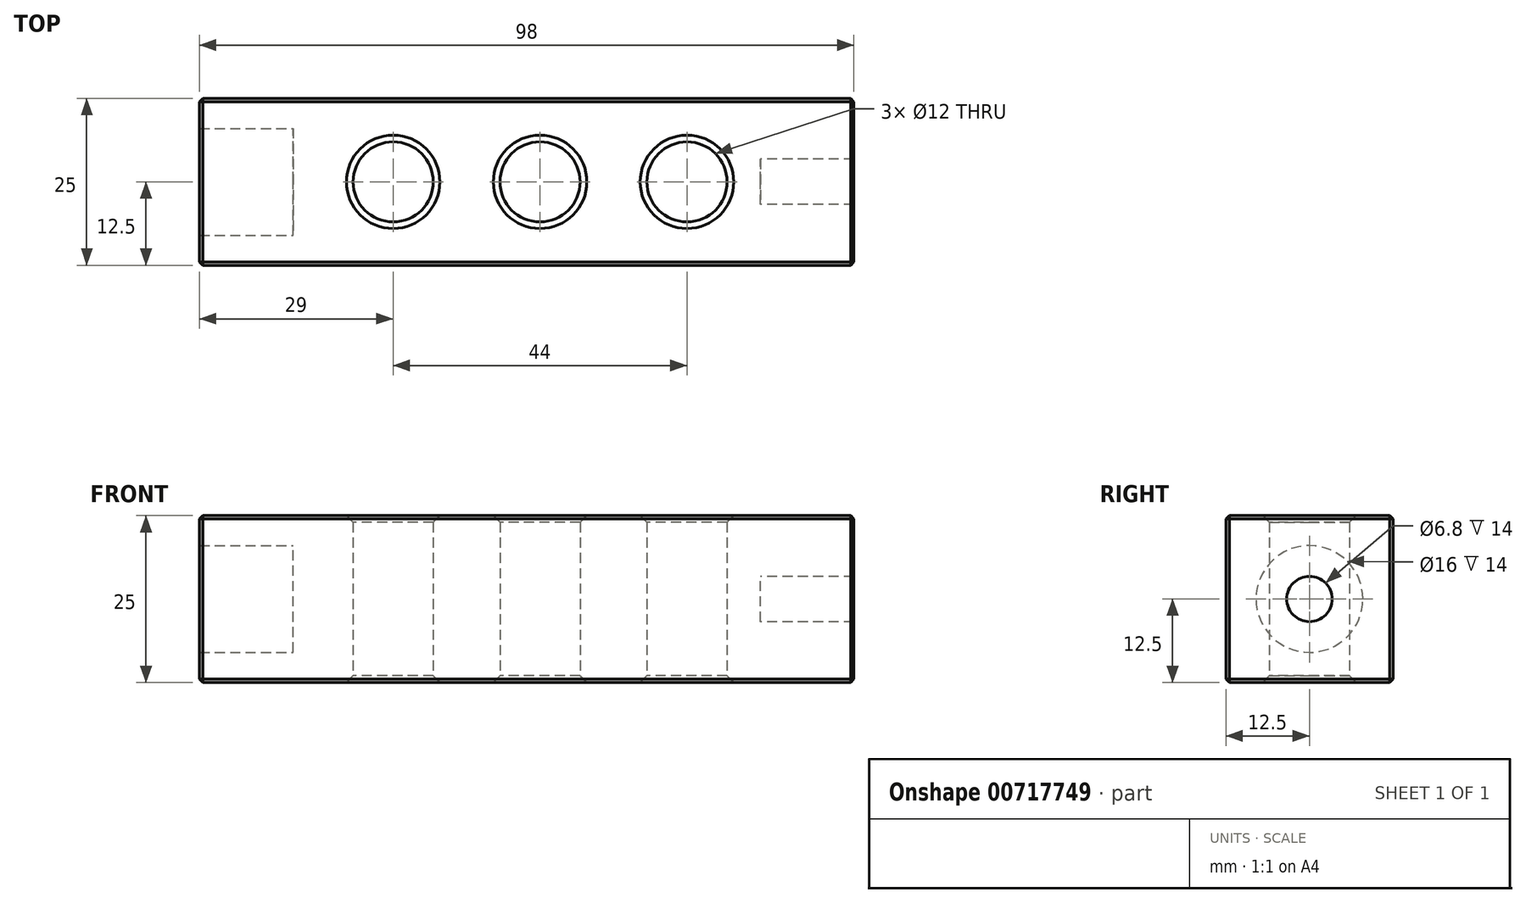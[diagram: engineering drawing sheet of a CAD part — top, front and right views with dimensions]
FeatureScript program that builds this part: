
annotation { "Feature Type Name" : "Feature", "Feature Type Description" : "" }
export const myFeature = defineFeature(function(context is Context, id is Id, definition is map)
    precondition{}
    {
        {
            var Q0;
            Q0=qCreatedBy(makeId("Top.planeOp"),FACE);
            var sketch = newSketch(context, id + "F0", { "sketchPlane" : qUnion([Q0])});
            skLineSegment(sketch, "E0.bottom", {"start": v(49, 12.5) * mm, "end": v(-49, 12.5) * mm});
            skLineSegment(sketch, "E0.top", {"start": v(49, -12.5) * mm, "end": v(-49, -12.5) * mm});
            skLineSegment(sketch, "E0.left", {"start": v(49, 12.5) * mm, "end": v(49, -12.5) * mm});
            skLineSegment(sketch, "E0.right", {"start": v(-49, 12.5) * mm, "end": v(-49, -12.5) * mm});
            skPoint(sketch, "E0.middle", {"position": v(0, 0) * mm});
            skLineSegment(sketch, "E1", {"start": v(49, 0) * mm, "end": v(-49, 0) * mm, "construction": true});
            skLineSegment(sketch, "E2", {"start": v(49, 12.5) * mm, "end": v(49, 22.83) * mm, "construction": true});
            skLineSegment(sketch, "E3", {"start": v(49, 22.83) * mm, "end": v(24, 22.83) * mm, "construction": true});
            skLineSegment(sketch, "E4", {"start": v(24, 22.83) * mm, "end": v(24, -3.88) * mm, "construction": true});
            skCircle(sketch, "E5", {"center": v(24, 0) * mm, "radius": 6 * mm});
            skCircle(sketch, "E6.1.0.0", {"center": v(2, 0) * mm, "radius": 6 * mm});
            skCircle(sketch, "E6.2.0.0", {"center": v(-20, 0) * mm, "radius": 6 * mm});
            skLineSegment(sketch, "E6.direction1", {"start": v(24, 0) * mm, "end": v(2, 0) * mm, "construction": true});
            skSolve(sketch);
        }
        {
            var Q0;
            Q0=makeQuery(id+"F0.imprint","IMPRINT",FACE,{"disambiguationData":[TD([[makeQuery(id+"F0.imprint","IMPRINT",EDGE,{"derivedFrom":sQuery(id+"F0.wireOp",EDGE,"E0.bottom")}),1.0]])]});
            extrude(context, id + "F1", {"entities" : qUnion([Q0]), "depth" : 25 * mm});
        }
        {
            var Q0;
            Q0=qCreatedBy(makeId("Right.planeOp"),FACE);
            var sketch = newSketch(context, id + "F2", { "sketchPlane" : qUnion([Q0])});
            skLineSegment(sketch, "E7", {"start": v(0, 0) * mm, "end": v(0, 12.5) * mm, "construction": true});
            skCircle(sketch, "E8", {"center": v(0, 12.5) * mm, "radius": 3.4 * mm});
            skSolve(sketch);
        }
        {
            var Q0;
            Q0=qSketchRegion(id+"F2",true);
            extrude(context, id + "F3", {"entities" : qUnion([Q0]), "operationType" : NewBodyOperationType.REMOVE, "depth" : 120 * mm, "hasSecondDirection" : true, "secondDirectionOppositeDirection" : true, "secondDirectionDepth" : -35 * mm, "offsetDistance" : 25 * mm});
        }
        {
            var Q0;
            Q0=qCreatedBy(makeId("Top.planeOp"),FACE);
            cPlane(context, id + "F4", {"entities" : qUnion([Q0]), "cplaneType" : CPlaneType.OFFSET, "offset" : 12.5 * mm, "width" : 150 * mm, "height" : 150 * mm});
        }
        {
            var Q0;
            Q0=qCreatedBy(id+"F4.planeOp",FACE);
            var sketch = newSketch(context, id + "F5", { "sketchPlane" : qUnion([Q0])});
            skLineSegment(sketch, "E9", {"start": v(0, 0) * mm, "end": v(100, 0) * mm, "construction": true});
            skArc(sketch, "E10", {"start": v(112.5, 0) * mm, "mid": v(100, 12.5) * mm, "end": v(87.5, 0) * mm});
            skLineSegment(sketch, "E11", {"start": v(100, 0) * mm, "end": v(112.5, 0) * mm});
            skLineSegment(sketch, "E12", {"start": v(100, 0) * mm, "end": v(87.5, 0) * mm});
            skSolve(sketch);
        }
        {
            var Q0;
            Q0=qCreatedBy(makeId("Right.planeOp"),FACE);
            var sketch = newSketch(context, id + "F6", { "sketchPlane" : qUnion([Q0])});
            skLineSegment(sketch, "E13", {"start": v(0, 0) * mm, "end": v(0, 12.5) * mm, "construction": true});
            skCircle(sketch, "E14", {"center": v(0, 12.5) * mm, "radius": 8 * mm});
            skSolve(sketch);
        }
        {
            var Q0;
            Q0=qSketchRegion(id+"F6",true);
            extrude(context, id + "F7", {"entities" : qUnion([Q0]), "operationType" : NewBodyOperationType.REMOVE, "oppositeDirection" : true, "depth" : 100 * mm, "hasSecondDirection" : true, "secondDirectionOppositeDirection" : true, "secondDirectionDepth" : 35 * mm, "offsetDistance" : 25 * mm});
        }
        {
            var Q0;
            Q0=makeQuery(id+"F1.opExtrude","SWEPT_EDGE",EDGE,{"disambiguationData":[OSD([sQuery(id+"F0.wireOp",EDGE,"E0.bottom"),sQuery(id+"F0.wireOp",EDGE,"E0.left")])]});
            var Q1;
            Q1=makeQuery(id+"F1.opExtrude","SWEPT_EDGE",EDGE,{"disambiguationData":[OSD([sQuery(id+"F0.wireOp",EDGE,"E0.top"),sQuery(id+"F0.wireOp",EDGE,"E0.left")])]});
            var Q2;
            Q2=makeQuery(id+"F1.opExtrude","CAP_EDGE",EDGE,{"disambiguationData":[OSD([sQuery(id+"F0.wireOp",EDGE,"E0.left")])],"isStart":true});
            var Q3;
            Q3=makeQuery(id+"F1.opExtrude","CAP_EDGE",EDGE,{"disambiguationData":[OSD([sQuery(id+"F0.wireOp",EDGE,"E0.left")])],"isStart":false});
            var Q4;
            Q4=makeQuery(id+"F1.opExtrude","CAP_EDGE",EDGE,{"disambiguationData":[OSD([sQuery(id+"F0.wireOp",EDGE,"E0.right")])],"isStart":false});
            var Q5;
            Q5=makeQuery(id+"F1.opExtrude","CAP_EDGE",EDGE,{"disambiguationData":[OSD([sQuery(id+"F0.wireOp",EDGE,"E0.bottom")])],"isStart":false});
            var Q6;
            Q6=makeQuery(id+"F1.opExtrude","CAP_EDGE",EDGE,{"disambiguationData":[OSD([sQuery(id+"F0.wireOp",EDGE,"E0.top")])],"isStart":false});
            var Q7;
            Q7=makeQuery(id+"F1.opExtrude","CAP_EDGE",EDGE,{"disambiguationData":[OSD([sQuery(id+"F0.wireOp",EDGE,"E0.top")])],"isStart":true});
            var Q8;
            Q8=makeQuery(id+"F1.opExtrude","SWEPT_EDGE",EDGE,{"disambiguationData":[OSD([sQuery(id+"F0.wireOp",EDGE,"E0.top"),sQuery(id+"F0.wireOp",EDGE,"E0.right")])]});
            var Q9;
            Q9=makeQuery(id+"F1.opExtrude","CAP_EDGE",EDGE,{"disambiguationData":[OSD([sQuery(id+"F0.wireOp",EDGE,"E0.right")])],"isStart":true});
            var Q10;
            Q10=makeQuery(id+"F1.opExtrude","SWEPT_EDGE",EDGE,{"disambiguationData":[OSD([sQuery(id+"F0.wireOp",EDGE,"E0.bottom"),sQuery(id+"F0.wireOp",EDGE,"E0.right")])]});
            var Q11;
            Q11=makeQuery(id+"F1.opExtrude","CAP_EDGE",EDGE,{"disambiguationData":[OSD([sQuery(id+"F0.wireOp",EDGE,"E0.bottom")])],"isStart":true});
            chamfer(context, id + "F8", {"entities" : qUnion([Q0, Q1, Q2, Q3, Q4, Q5, Q6, Q7, Q8, Q9, Q10, Q11]), "width" : .5 * mm, "tangentPropagation" : true});
        }
        {
            var Q0;
            Q0=makeQuery(id+"F1.opExtrude","CAP_EDGE",EDGE,{"disambiguationData":[OSD([sQuery(id+"F0.wireOp",EDGE,"E6.1.0.0")])],"isStart":true});
            var Q1;
            Q1=makeQuery(id+"F1.opExtrude","CAP_EDGE",EDGE,{"disambiguationData":[OSD([sQuery(id+"F0.wireOp",EDGE,"E5")])],"isStart":true});
            var Q2;
            Q2=makeQuery(id+"F1.opExtrude","CAP_EDGE",EDGE,{"disambiguationData":[OSD([sQuery(id+"F0.wireOp",EDGE,"E6.2.0.0")])],"isStart":true});
            var Q3;
            Q3=makeQuery(id+"F1.opExtrude","CAP_EDGE",EDGE,{"disambiguationData":[OSD([sQuery(id+"F0.wireOp",EDGE,"E6.2.0.0")])],"isStart":false});
            var Q4;
            Q4=makeQuery(id+"F1.opExtrude","CAP_EDGE",EDGE,{"disambiguationData":[OSD([sQuery(id+"F0.wireOp",EDGE,"E6.1.0.0")])],"isStart":false});
            var Q5;
            Q5=makeQuery(id+"F1.opExtrude","CAP_EDGE",EDGE,{"disambiguationData":[OSD([sQuery(id+"F0.wireOp",EDGE,"E5")])],"isStart":false});
            chamfer(context, id + "F9", {"entities" : qUnion([Q0, Q1, Q2, Q3, Q4, Q5]), "width" : 1 * mm, "tangentPropagation" : true});
        }
    });
